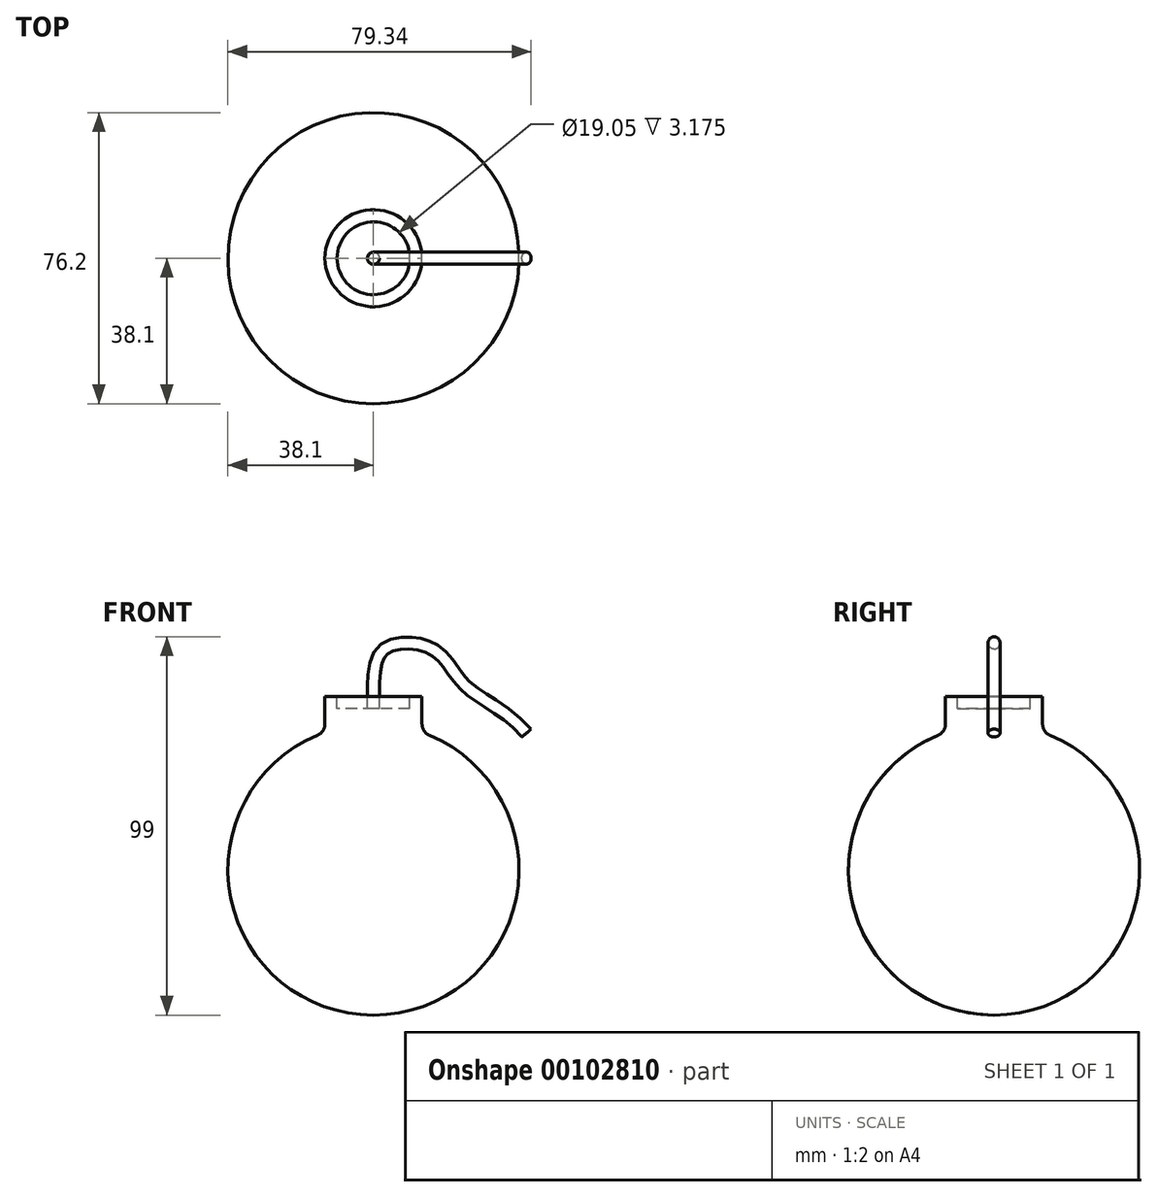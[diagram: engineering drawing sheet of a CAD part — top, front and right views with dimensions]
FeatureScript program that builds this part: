
annotation { "Feature Type Name" : "Feature", "Feature Type Description" : "" }
export const myFeature = defineFeature(function(context is Context, id is Id, definition is map)
    precondition{}
    {
        {
            var Q0;
            Q0=qCreatedBy(makeId("Right.planeOp"),FACE);
            var sketch = newSketch(context, id + "F0", { "sketchPlane" : qUnion([Q0])});
            skArc(sketch, "E0", {"start": v(0, 38.1) * mm, "mid": v(-38.1, 0) * mm, "end": v(0, -38.1) * mm});
            skLineSegment(sketch, "E1", {"start": v(0, 64.9) * mm, "end": v(0, -66.83) * mm});
            skSolve(sketch);
        }
        {
            var Q0;
            {var subQ0=sQuery(id+"F0.wireOp",EDGE,"E0");Q0=makeQuery(id+"F0.imprint","IMPRINT",FACE,{"disambiguationData":[TD([[makeQuery(id+"F0.imprint","IMPRINT",EDGE,{"derivedFrom":subQ0}),1.0]])]});}
            var Q1;
            Q1=sQuery(id+"F0.wireOp",EDGE,"E1");
            revolve(context, id + "F1", {"entities" : qUnion([Q0]), "axis" : qUnion([Q1]), "revolveType" : RevolveType.FULL, "oppositeDirection" : true});
        }
        {
            var Q0;
            Q0=qCreatedBy(makeId("Top.planeOp"),FACE);
            var sketch = newSketch(context, id + "F2", { "sketchPlane" : qUnion([Q0])});
            skCircle(sketch, "E2", {"center": v(0, 0) * mm, "radius": 12.7 * mm});
            skSolve(sketch);
        }
        {
            var Q0;
            Q0 = qSketchRegion(id + "F2", true);
            extrude(context, id + "F3", {"entities" : qUnion([Q0]), "operationType" : NewBodyOperationType.ADD, "depth" : 45.35 * mm});
        }
        {
            var Q0;
            Q0=makeQuery(id+"F3.opExtrude","CAP_FACE",FACE,{"disambiguationData":[OSD([sQuery(id+"F2.wireOp",EDGE,"E2")])],"isStart":false});
            var sketch = newSketch(context, id + "F4", { "sketchPlane" : qUnion([Q0])});
            skCircle(sketch, "E3", {"center": v(0, 0) * mm, "radius": 9.53 * mm});
            skSolve(sketch);
        }
        {
            var Q0;
            Q0 = qSketchRegion(id + "F4", true);
            extrude(context, id + "F5", {"entities" : qUnion([Q0]), "operationType" : NewBodyOperationType.REMOVE, "oppositeDirection" : true, "depth" : 3.17 * mm});
        }
        {
            var Q0;
            Q0=makeQuery(id+"F3.boolean.opBoolean","INTERSECT",EDGE,{"derivedFrom":[makeQuery(id+"F1.opRevolve","SWEPT_FACE",FACE,{"disambiguationData":[OSD([sQuery(id+"F0.wireOp",EDGE,"E0")])]}),makeQuery(id+"F3.opExtrude","SWEPT_FACE",FACE,{"disambiguationData":[OSD([sQuery(id+"F2.wireOp",EDGE,"E2")])]})]});
            fillet(context, id + "F6", {"entities" : qUnion([Q0]), "radius" : 3.17 * mm, "allowEdgeOverflow" : false});
        }
        {
            var Q0;
            Q0=makeQuery(id+"F5.boolean.opBoolean","COPY",FACE,{"derivedFrom":makeQuery(id+"F5.opExtrude","CAP_FACE",FACE,{"disambiguationData":[OSD([sQuery(id+"F4.wireOp",EDGE,"E3")])],"isStart":false})});
            var sketch = newSketch(context, id + "F7", { "sketchPlane" : qUnion([Q0])});
            skCircle(sketch, "E4", {"center": v(0, 0) * mm, "radius": 1.59 * mm});
            skSolve(sketch);
        }
        {
            var Q0;
            Q0=qCreatedBy(makeId("Front.planeOp"),FACE);
            var sketch = newSketch(context, id + "F8", { "sketchPlane" : qUnion([Q0])});
            skFitSpline(sketch, "E5", {"points": [v(0, 37.45) * mm, v(3.28, 58.05) * mm, v(15.76, 57.55) * mm, v(23.92, 48.28) * mm, v(40.05, 35.75) * mm], "startDerivative": vector(0, 129.41) * mm, "endDerivative": vector(60.12, -69.23) * mm});
            skSolve(sketch);
        }
        {
            var Q0;
            Q0=makeQuery(id+"F7.imprint","IMPRINT",FACE,{"disambiguationData":[TD([[makeQuery(id+"F7.imprint","IMPRINT",EDGE,{"derivedFrom":sQuery(id+"F7.wireOp",EDGE,"E4")}),1.0]])]});
            var Q1;
            Q1=sQuery(id+"F8.wireOp",EDGE,"E5");
            sweep(context, id + "F9", {"operationType" : NewBodyOperationType.ADD, "profiles" : qUnion([Q0]), "path" : qUnion([Q1])});
        }
    });
